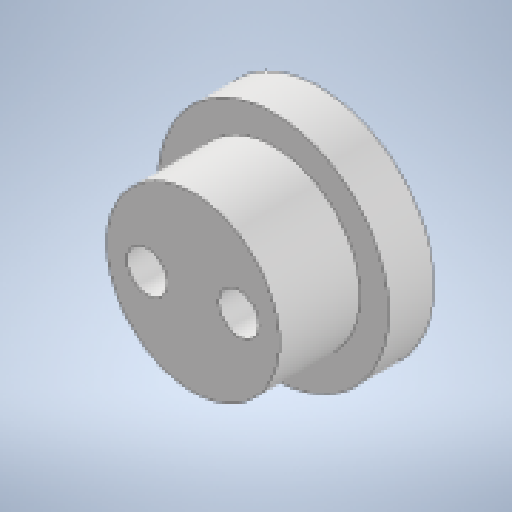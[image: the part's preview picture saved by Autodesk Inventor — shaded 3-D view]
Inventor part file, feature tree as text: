
AUTODESK INVENTOR PART (.ipt)
format: ipt  version: 2023 (Build 270158000, 158)  size: 154,624 bytes
history: native  units: in
note: dims shown in document units (in); Inventor stores cm internally (conversion verified against a paired STEP export)
features: other x3, extrude x2, sketch x2, reference x1
ambient origin geometry x8: Origin, YZ Plane, XZ Plane, XY Plane, X Axis, Y Axis, Z Axis, Center Point
bodies: Solid1 (feature_tree)
feature tree (8):
  extrude  "Extrusion1"  Depth=0.1554in TaperAngle=0.0deg
  extrude  "Extrusion2"  Depth=0.2756in TaperAngle=0.0deg
  sketch  "Sketch1"  dims[d0=0.7874in d1=0.1554in d2=0.0in]
  reference  "Reference1"
  sketch  "Sketch2"  dims[d3=0.5906in d4=0.2756in d5=0.0in d6=0.315in]
  other  "<userpath>\OneDrive\Documents\Robotics Club\Cycloidal Drive\Drive.iam"
  other  "Drive.iam"
  other  "Shaft-3:1"
